# Revit family: RN 55034 Optipress-Therm-Übergang
name_source: partatom
category: Rohrformteile
units: mm (PartAtom-declared; Revit-internal decimal feet)

## family parameters
Arbeitsebenenbasiert = Nein
Beim Laden mit Abzugskörper schneiden = Nein
Bemaßung runder Anschluss = Durchmesser verwenden
Gemeinsam genutzt = Nein
Immer vertikal = Ja
Teiletyp = Verbindung

## types (6) — shared parameters
1.010.00.2 Blattnummer der Richtlinie = 29
1.010.00.3 Ausgabedatum (Monat) der Richtlinie = 201308
1.010.00.4 Herstellername = R. Nussbaum AG
1.010.00.5 Revisionsdatum der Datei = 20190521
1.010.00.6 Webadresse des Herstellers = http://www.nussbaum.ch
1.100.00.4 Produktbezeichnung = Versorgung
1.110.00.2 Index = 1
1.110.00.4 Produktbezeichnung = Optipress-Therm
1.960/3L.00.8 Link (URL) = https://www.nussbaum.ch
29.700.00.4 Produktname = Optipress-Therm-Übergang, mit Einsteckende und Innengewinde
29.700.00.5 Produktkennung = 2
29.700.00.6 Querschnittsform = 1
29.700.00.7 Nennweitensystem = DN
29.700.00.8 Nenndrucksystem = PN
29.710.02.4 Nenndruck = 16
29.710.02.5 max. zul. Überdruck [hPa] = 1600
29.710.02.7 max. zul. Dauer-Betriebsdruck [hPa] = 1600
29.710.02.9 max. zul. Dauer-Betriebstemperatur [°C] = 95
Connector Visibility = Nein
EnclosingSpace Visibility = Nein
Hersteller = R. Nussbaum AG

## per-type parameters (varying)
| type | 1.800.00.3 TGA-Nummer | 1.800.00.4 Kommentarfeld | 1.810.00.3 Hersteller-Bestellnummer | 1.810.00.4 DATANORM-Nummer | 1.810.00.5 StLB-Nummer | 1.810.00.6 GTIN-Nummer | 29.710.02.10 Formstück-Gewicht [kg] | 29.710.02.3 Benennung | CONNECTOR0_DIAMETER_dX_0r | CONNECTOR0_dX_01 | CONNECTOR0_ref_dX | CONNECTOR1_DIAMETER_dX_0r | CONNECTOR1_dX_00 | CONNECTOR1_dX_01 | CONNECTOR1_ref_dX | Modell | R. Nussbaum AG 55034.22 de Visibility | R. Nussbaum AG 55034.23 de Visibility | R. Nussbaum AG 55034.24 de Visibility | R. Nussbaum AG 55034.25 de Visibility | R. Nussbaum AG 55034.26 de Visibility | R. Nussbaum AG 55034.27 de Visibility | Typenkommentare |
| DN=25 | 01900100000000000000000000000000000000000000000021000000000000000006 | 55034.27, Optipress-Therm-Übergang, mit Einsteckende und Innengewinde, DN=25, L=49, Rp=1 | 55034.27 | 55034.27 |  | 7612945708977 | 0.078 | Optipress-Therm-Übergang, mit Einsteckende und Innengewinde, DN=25, L=49, Rp=1 | 25 mm  [stored 0.082021 ft] | 24 mm | 24 mm | 25 mm  [stored 0.082021 ft] | 32 mm | 49 mm | 32 mm | 55034.27 | Nein | Nein | Nein | Nein | Nein | Ja | Optipress-Therm-Übergang DN=25 |
| DN=20 | 01900100000000000000000000000000000000000000000021000000000000000005 | 55034.26, Optipress-Therm-Übergang, mit Einsteckende und Innengewinde, DN=20, L=50, Rp=¾ | 55034.26 | 55034.26 | 255.704 | 7612945663849 | 0.073 | Optipress-Therm-Übergang, mit Einsteckende und Innengewinde, DN=20, L=50, Rp=¾ | 20 mm | 24 mm | 24 mm | 20 mm | 35 mm | 50 mm | 35 mm | 55034.26 | Nein | Nein | Nein | Nein | Ja | Nein | Optipress-Therm-Übergang DN=20 |
| DN=20x15 | 01900100000000000000000000000000000000000000000021000000000000000004 | 55034.25, Optipress-Therm-Übergang, mit Einsteckende und Innengewinde, DN=20x15, L=46, Rp=½ | 55034.25 | 55034.25 | 255.704 | 7612945663825 | 0.059 | Optipress-Therm-Übergang, mit Einsteckende und Innengewinde, DN=20x15, L=46, Rp=½ | 20 mm | 24 mm | 24 mm | 15 mm | 33 mm  [stored 0.108268 ft] | 46 mm | 33 mm  [stored 0.108268 ft] | 55034.25 | Nein | Nein | Nein | Ja | Nein | Nein | Optipress-Therm-Übergang DN=20x15 |
| DN=15x20 | 01900100000000000000000000000000000000000000000021000000000000000003 | 55034.24, Optipress-Therm-Übergang, mit Einsteckende und Innengewinde, DN=15x20, L=51, Rp=¾ | 55034.24 | 55034.24 | 255.703 | 7612945663801 | 0.078 | Optipress-Therm-Übergang, mit Einsteckende und Innengewinde, DN=15x20, L=51, Rp=¾ | 15 mm | 22 mm | 22 mm | 20 mm | 36 mm | 51 mm | 36 mm | 55034.24 | Nein | Nein | Ja | Nein | Nein | Nein | Optipress-Therm-Übergang DN=15x20 |
| DN=15 | 01900100000000000000000000000000000000000000000021000000000000000002 | 55034.23, Optipress-Therm-Übergang, mit Einsteckende und Innengewinde, DN=15, L=46, Rp=½ | 55034.23 | 55034.23 | 255.703 | 7612945663788 | 0.053 | Optipress-Therm-Übergang, mit Einsteckende und Innengewinde, DN=15, L=46, Rp=½ | 15 mm | 22 mm | 22 mm | 15 mm | 33 mm  [stored 0.108268 ft] | 46 mm | 33 mm  [stored 0.108268 ft] | 55034.23 | Nein | Ja | Nein | Nein | Nein | Nein | Optipress-Therm-Übergang DN=15 |
| DN=12x15 | 01900100000000000000000000000000000000000000000021000000000000000001 | 55034.22, Optipress-Therm-Übergang, mit Einsteckende und Innengewinde, DN=12x15, L=47, Rp=½ | 55034.22 | 55034.22 | 255.702 | 7612945663764 | 0.058 | Optipress-Therm-Übergang, mit Einsteckende und Innengewinde, DN=12x15, L=47, Rp=½ | 12 mm  [stored 0.0393701 ft] | 22 mm | 22 mm | 15 mm | 34 mm | 47 mm | 34 mm | 55034.22 | Ja | Nein | Nein | Nein | Nein | Nein | Optipress-Therm-Übergang DN=12x15 |

note: [stored X ft] marks values corroborated as IEEE doubles in the binary element streams (Revit-internal decimal feet)
